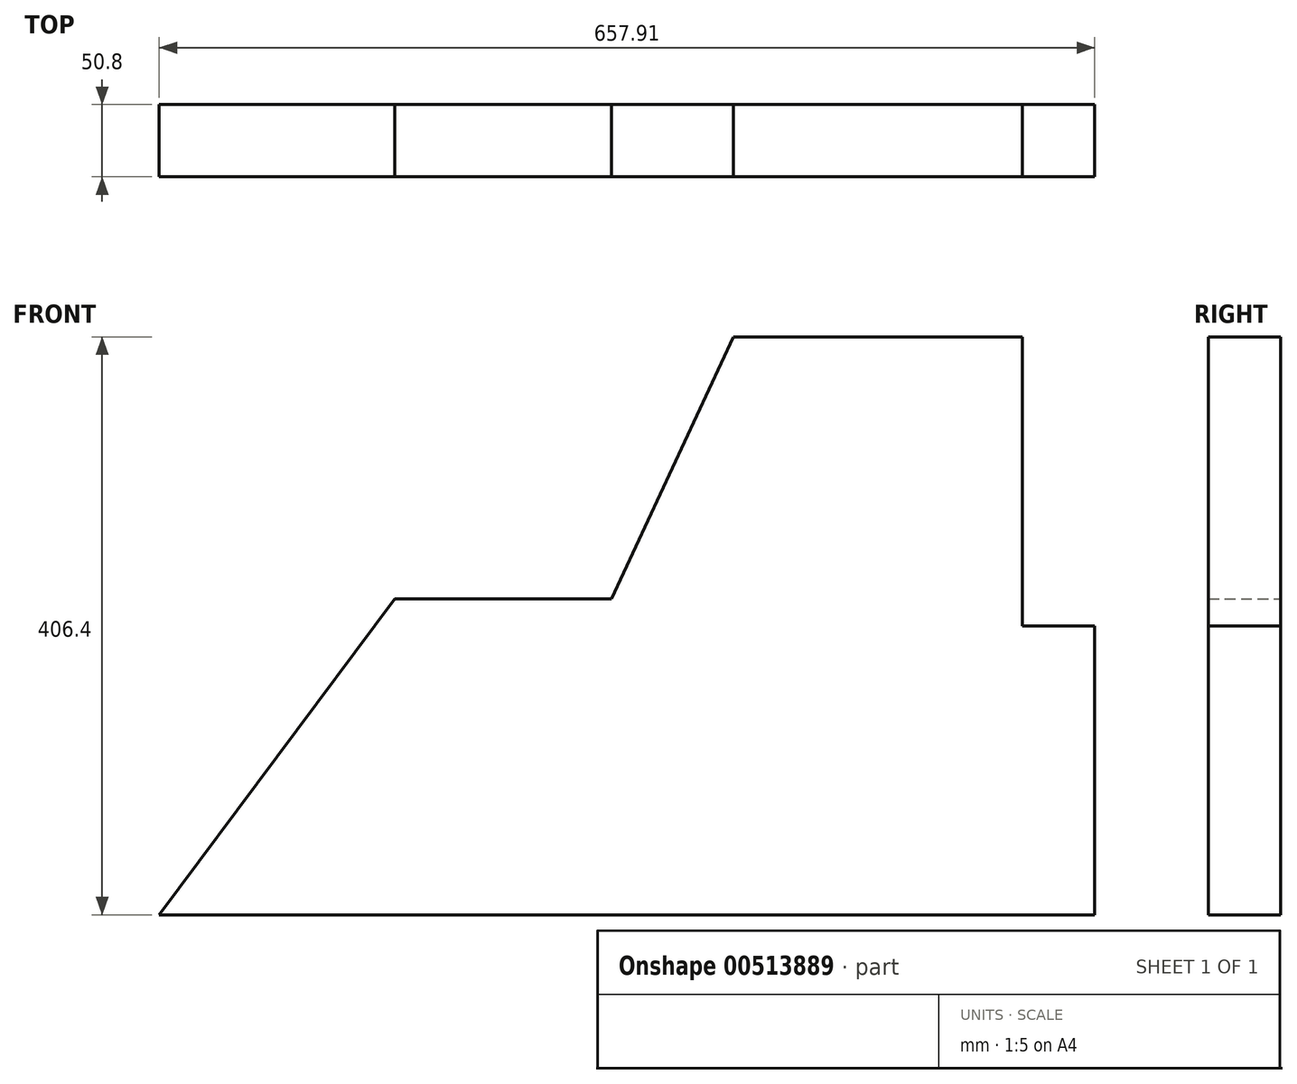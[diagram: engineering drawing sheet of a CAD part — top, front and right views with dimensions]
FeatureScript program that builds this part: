
annotation { "Feature Type Name" : "Feature", "Feature Type Description" : "" }
export const myFeature = defineFeature(function(context is Context, id is Id, definition is map)
    precondition{}
    {
        {
            var Q0;
            Q0=qCreatedBy(makeId("Front.planeOp"),FACE);
            var sketch = newSketch(context, id + "F0", { "sketchPlane" : qUnion([Q0])});
            skLineSegment(sketch, "E0", {"start": v(-2.49, 0) * mm, "end": v(657.91, 0) * mm});
            skLineSegment(sketch, "E1", {"start": v(657.91, 0) * mm, "end": v(657.91, 203.2) * mm});
            skLineSegment(sketch, "E2", {"start": v(657.91, 203.2) * mm, "end": v(607.11, 203.2) * mm});
            skLineSegment(sketch, "E3", {"start": v(607.11, 203.2) * mm, "end": v(607.11, 406.4) * mm});
            skLineSegment(sketch, "E4", {"start": v(607.11, 406.4) * mm, "end": v(403.91, 406.4) * mm});
            skLineSegment(sketch, "E5", {"start": v(403.91, 406.4) * mm, "end": v(318.15, 222.19) * mm});
            skLineSegment(sketch, "E6", {"start": v(318.15, 222.19) * mm, "end": v(165.75, 222.19) * mm});
            skLineSegment(sketch, "E7", {"start": v(165.75, 222.19) * mm, "end": v(0, 0) * mm});
            skSolve(sketch);
        }
        {
            var Q0;
            {var subQ0=sQuery(id+"F0.wireOp",EDGE,"E1");Q0=makeQuery(id+"F0.imprint","IMPRINT",FACE,{"disambiguationData":[TD([[makeQuery(id+"F0.imprint","IMPRINT",EDGE,{"derivedFrom":subQ0}),1.0]])]});}
            extrude(context, id + "F1", {"entities" : qUnion([Q0]), "depth" : 50.8 * mm, "offsetDistance" : 25.4 * mm});
        }
    });
